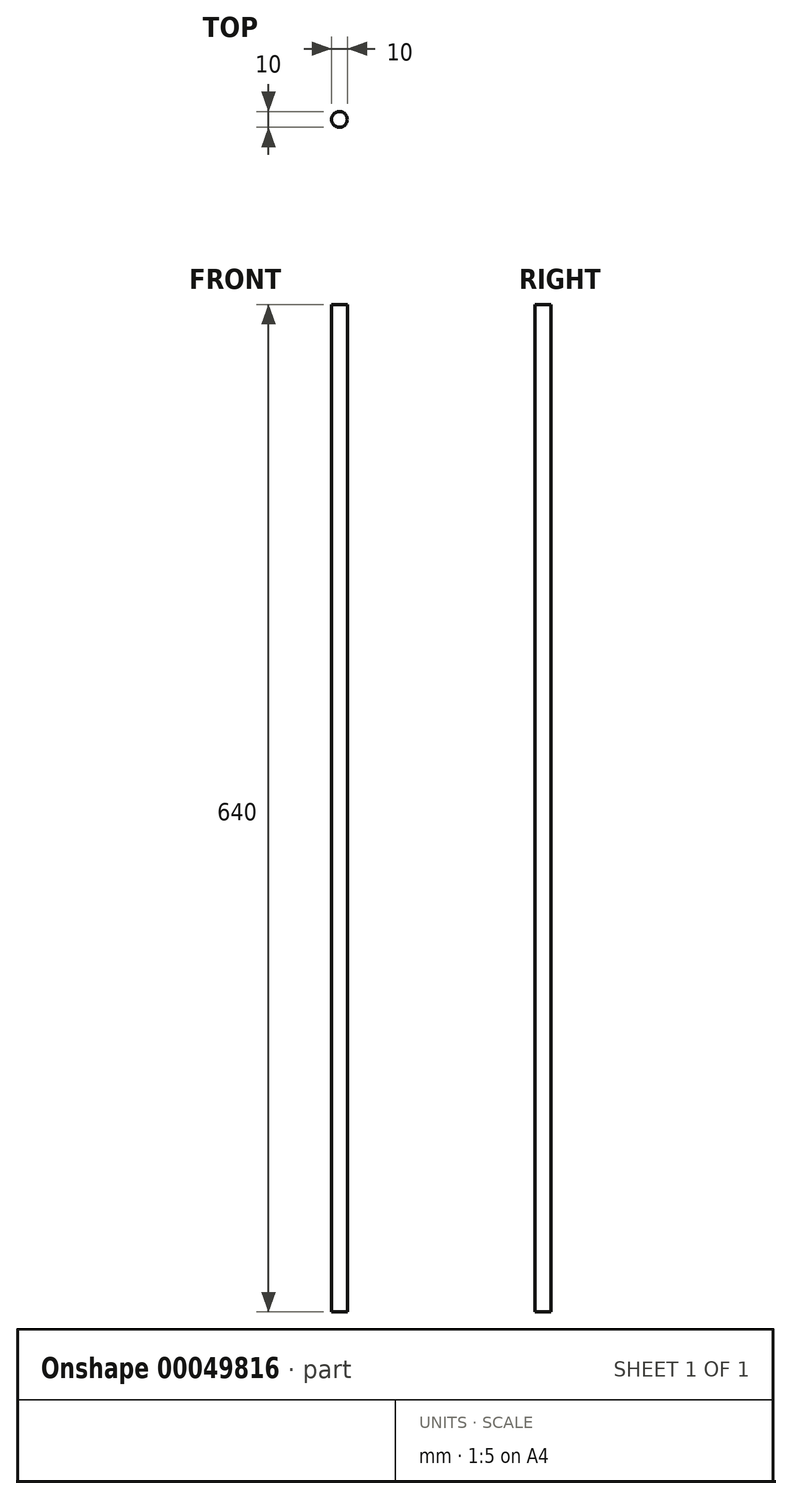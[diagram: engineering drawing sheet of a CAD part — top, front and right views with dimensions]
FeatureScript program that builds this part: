
annotation { "Feature Type Name" : "Feature", "Feature Type Description" : "" }
export const myFeature = defineFeature(function(context is Context, id is Id, definition is map)
    precondition{}
    {
        {
            var Q0;
            Q0=qCreatedBy(makeId("Top.planeOp"),FACE);
            var sketch = newSketch(context, id + "F0", { "sketchPlane" : qUnion([Q0])});
            skCircle(sketch, "E0", {"center": v(0, 0) * mm, "radius": 5 * mm});
            skSolve(sketch);
        }
        {
            var Q0;
            Q0=qSketchRegion(id+"F0",true);
            extrude(context, id + "F1", {"entities" : qUnion([Q0]), "depth" : 640 * mm});
        }
    });
